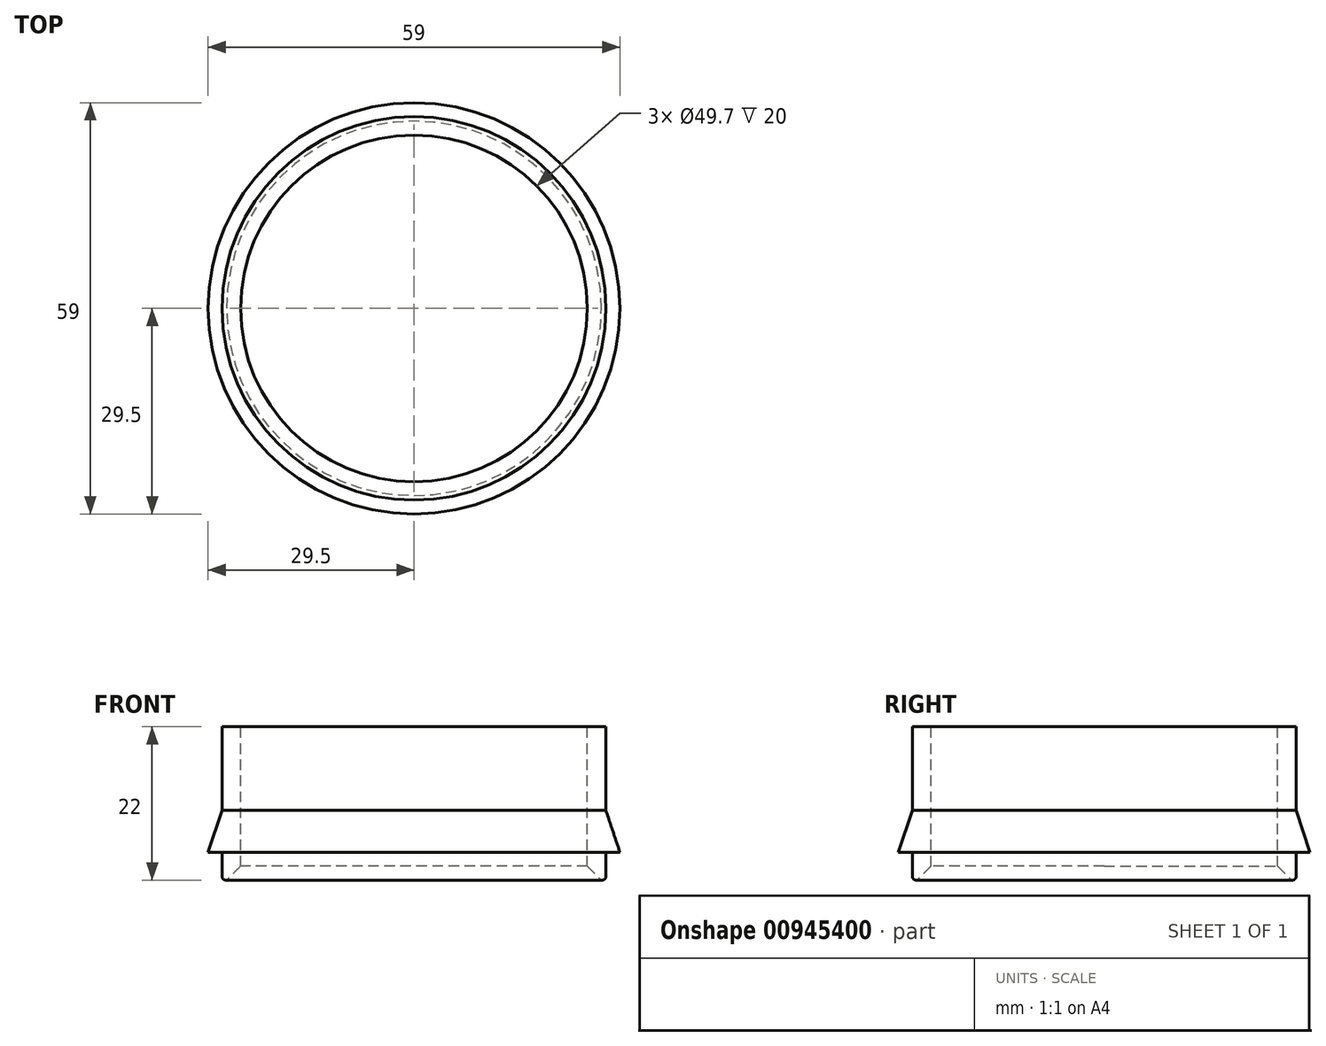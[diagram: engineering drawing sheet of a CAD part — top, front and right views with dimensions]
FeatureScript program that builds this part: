
annotation { "Feature Type Name" : "Feature", "Feature Type Description" : "" }
export const myFeature = defineFeature(function(context is Context, id is Id, definition is map)
    precondition{}
    {
        {
            var Q0;
            Q0=qCreatedBy(makeId("Front.planeOp"),FACE);
            var sketch = newSketch(context, id + "F0", { "sketchPlane" : qUnion([Q0])});
            skLineSegment(sketch, "E0", {"start": v(24.85, 0) * mm, "end": v(27.5, 0) * mm});
            skLineSegment(sketch, "E1", {"start": v(27.5, 0) * mm, "end": v(27.5, -12) * mm});
            skLineSegment(sketch, "E2", {"start": v(27.5, -12) * mm, "end": v(29.5, -18) * mm});
            skLineSegment(sketch, "E3", {"start": v(29.5, -18) * mm, "end": v(27.5, -18) * mm});
            skLineSegment(sketch, "E4", {"start": v(27.5, -18) * mm, "end": v(27.5, -22) * mm});
            skLineSegment(sketch, "E5", {"start": v(27.5, -22) * mm, "end": v(24.85, -22) * mm});
            skLineSegment(sketch, "E6", {"start": v(24.85, -22) * mm, "end": v(24.85, 0) * mm});
            skLineSegment(sketch, "E7", {"start": v(0, 0) * mm, "end": v(0, -12.37) * mm, "construction": true});
            skSolve(sketch);
        }
        {
            var Q0;
            Q0=makeQuery(id+"F0.imprint","IMPRINT",FACE,{"disambiguationData":[TD([[makeQuery(id+"F0.imprint","IMPRINT",EDGE,{"derivedFrom":sQuery(id+"F0.wireOp",EDGE,"E0")}),-1.0]])]});
            var Q1;
            Q1=sQuery(id+"F0.wireOp",EDGE,"E7");
            revolve(context, id + "F1", {"surfaceOperationType" : NewSurfaceOperationType.NEW, "entities" : qUnion([Q0]), "axis" : qUnion([Q1]), "revolveType" : RevolveType.FULL});
        }
        {
            var Q0;
            Q0=makeQuery(id+"F1.opRevolve","SWEPT_EDGE",EDGE,{"disambiguationData":[OSD([sQuery(id+"F0.wireOp",EDGE,"E4"),sQuery(id+"F0.wireOp",EDGE,"E5")])]});
            fillet(context, id + "F2", {"entities" : qUnion([Q0]), "radius" : .5 * mm, "tangentPropagation" : true, "allowEdgeOverflow" : false});
        }
        {
            var Q0;
            Q0=makeQuery(id+"F1.opRevolve","SWEPT_EDGE",EDGE,{"disambiguationData":[OSD([sQuery(id+"F0.wireOp",EDGE,"E5"),sQuery(id+"F0.wireOp",EDGE,"E6")])]});
            chamfer(context, id + "F3", {"entities" : qUnion([Q0]), "width" : 2 * mm, "tangentPropagation" : true});
        }
    });
